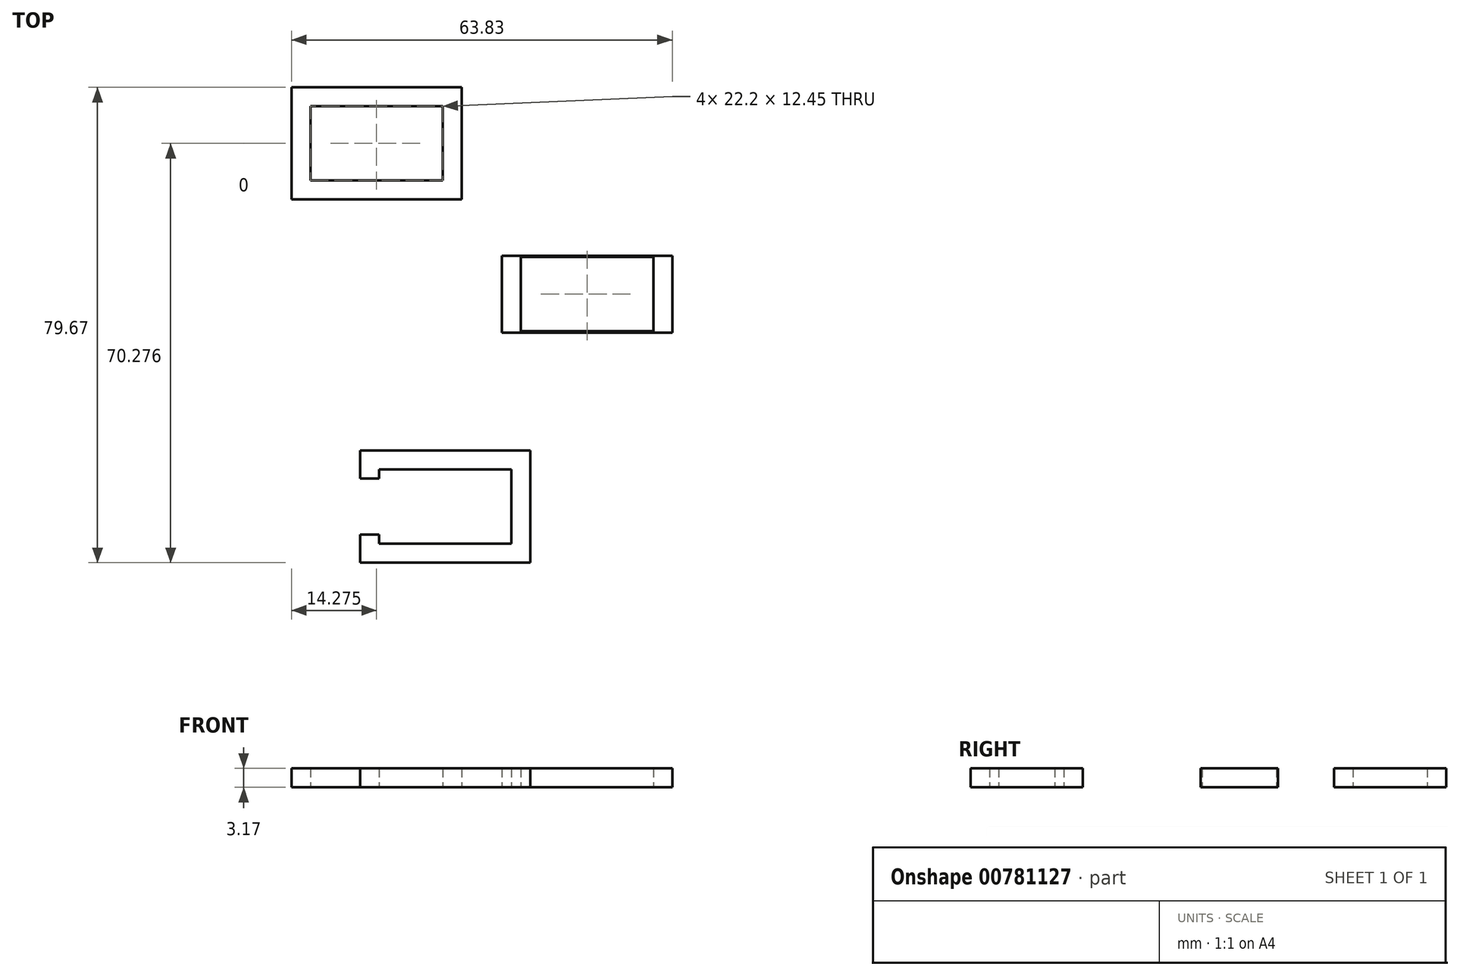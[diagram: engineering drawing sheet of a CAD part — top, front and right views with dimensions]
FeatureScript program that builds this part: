
annotation { "Feature Type Name" : "Feature", "Feature Type Description" : "" }
export const myFeature = defineFeature(function(context is Context, id is Id, definition is map)
    precondition{}
    {
        {
            var Q0;
            Q0=qCreatedBy(makeId("Top.planeOp"),FACE);
            var sketch = newSketch(context, id + "F0", { "sketchPlane" : qUnion([Q0])});
            skLineSegment(sketch, "E0.bottom", {"start": v(11.1, -6.22) * mm, "end": v(-11.1, -6.22) * mm});
            skLineSegment(sketch, "E0.top", {"start": v(11.1, 6.22) * mm, "end": v(-11.1, 6.22) * mm});
            skLineSegment(sketch, "E0.left", {"start": v(11.1, -6.22) * mm, "end": v(11.1, 6.22) * mm});
            skLineSegment(sketch, "E0.right", {"start": v(-11.1, -6.22) * mm, "end": v(-11.1, 6.22) * mm});
            skPoint(sketch, "E0.middle", {"position": v(0, 0) * mm});
            skLineSegment(sketch, "E1.bottom", {"start": v(14.27, -6.44) * mm, "end": v(-14.27, -6.44) * mm});
            skLineSegment(sketch, "E1.top", {"start": v(14.27, 6.44) * mm, "end": v(-14.27, 6.44) * mm});
            skLineSegment(sketch, "E1.left", {"start": v(14.27, -6.44) * mm, "end": v(14.27, 6.44) * mm});
            skLineSegment(sketch, "E1.right", {"start": v(-14.27, -6.44) * mm, "end": v(-14.27, 6.44) * mm});
            skLineSegment(sketch, "E2.bottom", {"start": v(-12.68, -41.84) * mm, "end": v(-34.87, -41.84) * mm});
            skLineSegment(sketch, "E2.top", {"start": v(-12.68, -29.39) * mm, "end": v(-34.87, -29.39) * mm});
            skLineSegment(sketch, "E2.left", {"start": v(-12.68, -41.84) * mm, "end": v(-12.68, -29.39) * mm});
            skLineSegment(sketch, "E2.right", {"start": v(-34.87, -41.84) * mm, "end": v(-34.87, -40.31) * mm});
            skPoint(sketch, "E2.middle", {"position": v(-23.78, -35.61) * mm});
            skLineSegment(sketch, "E3.bottom", {"start": v(-9.5, -45.01) * mm, "end": v(-38.05, -45.01) * mm});
            skLineSegment(sketch, "E3.top", {"start": v(-9.5, -26.21) * mm, "end": v(-38.05, -26.21) * mm});
            skLineSegment(sketch, "E3.left", {"start": v(-9.5, -45.01) * mm, "end": v(-9.5, -26.21) * mm});
            skLineSegment(sketch, "E3.right", {"start": v(-38.05, -45.01) * mm, "end": v(-38.05, -40.31) * mm});
            skLineSegment(sketch, "E4", {"start": v(-38.05, -26.21) * mm, "end": v(-38.05, -30.91) * mm});
            skLineSegment(sketch, "E5", {"start": v(-38.05, -40.31) * mm, "end": v(-34.87, -40.31) * mm});
            skLineSegment(sketch, "E6", {"start": v(-38.05, -30.91) * mm, "end": v(-34.87, -30.91) * mm});
            skLineSegment(sketch, "E7.trimOffspring", {"start": v(-38.05, -30.91) * mm, "end": v(-38.05, -26.21) * mm});
            skPoint(sketch, "E8.orphan", {"position": v(-38.05, -35.61) * mm});
            skLineSegment(sketch, "E9.trimOffspring", {"start": v(-34.87, -30.91) * mm, "end": v(-34.87, -29.39) * mm});
            skLineSegment(sketch, "E10.bottom", {"start": v(-38.05, -26.21) * mm, "end": v(-9.5, -26.21) * mm});
            skLineSegment(sketch, "E10.top", {"start": v(-38.05, -45.01) * mm, "end": v(-9.5, -45.01) * mm});
            skLineSegment(sketch, "E10.left", {"start": v(-38.05, -26.21) * mm, "end": v(-38.05, -45.01) * mm});
            skLineSegment(sketch, "E10.right", {"start": v(-9.5, -26.21) * mm, "end": v(-9.5, -45.01) * mm});
            skLineSegment(sketch, "E11.bottom", {"start": v(-34.87, -29.39) * mm, "end": v(-12.68, -29.39) * mm});
            skLineSegment(sketch, "E11.top", {"start": v(-34.87, -41.84) * mm, "end": v(-12.68, -41.84) * mm});
            skLineSegment(sketch, "E11.left", {"start": v(-34.87, -29.39) * mm, "end": v(-34.87, -41.84) * mm});
            skLineSegment(sketch, "E11.right", {"start": v(-12.68, -29.39) * mm, "end": v(-12.68, -41.84) * mm});
            skLineSegment(sketch, "E12.bottom", {"start": v(-46.38, 31.49) * mm, "end": v(-24.18, 31.49) * mm});
            skLineSegment(sketch, "E12.top", {"start": v(-46.38, 19.04) * mm, "end": v(-24.18, 19.04) * mm});
            skLineSegment(sketch, "E12.left", {"start": v(-46.38, 31.49) * mm, "end": v(-46.38, 19.04) * mm});
            skLineSegment(sketch, "E12.right", {"start": v(-24.18, 31.49) * mm, "end": v(-24.18, 19.04) * mm});
            skLineSegment(sketch, "E13.bottom", {"start": v(-49.56, 34.66) * mm, "end": v(-21, 34.66) * mm});
            skLineSegment(sketch, "E13.top", {"start": v(-49.56, 15.87) * mm, "end": v(-21, 15.87) * mm});
            skLineSegment(sketch, "E13.left", {"start": v(-49.56, 34.66) * mm, "end": v(-49.56, 15.87) * mm});
            skLineSegment(sketch, "E13.right", {"start": v(-21, 34.66) * mm, "end": v(-21, 15.87) * mm});
            skSolve(sketch);
        }
        {
            var Q0;
            Q0=makeQuery(id+"F0.imprint","IMPRINT",FACE,{"disambiguationData":[TD([[makeQuery(id+"F0.imprint","IMPRINT",EDGE,{"derivedFrom":sQuery(id+"F0.wireOp",EDGE,"E2.bottom")}),1.0]])]});
            var Q1;
            Q1=makeQuery(id+"F0.imprint","IMPRINT",FACE,{"disambiguationData":[TD([[makeQuery(id+"F0.imprint","IMPRINT",EDGE,{"derivedFrom":sQuery(id+"F0.wireOp",EDGE,"E0.bottom")}),1.0]])]});
            extrude(context, id + "F1", {"entities" : qUnion([Q0, Q1]), "depth" : 3.17 * mm, "offsetDistance" : 25.4 * mm});
        }
        {
            var Q0;
            Q0=makeQuery(id+"F0.imprint","IMPRINT",FACE,{"disambiguationData":[TD([[makeQuery(id+"F0.imprint","IMPRINT",EDGE,{"derivedFrom":sQuery(id+"F0.wireOp",EDGE,"E12.bottom")}),1.0]])]});
            extrude(context, id + "F2", {"entities" : qUnion([Q0]), "depth" : 3.17 * mm, "offsetDistance" : 25.4 * mm});
        }
    });
